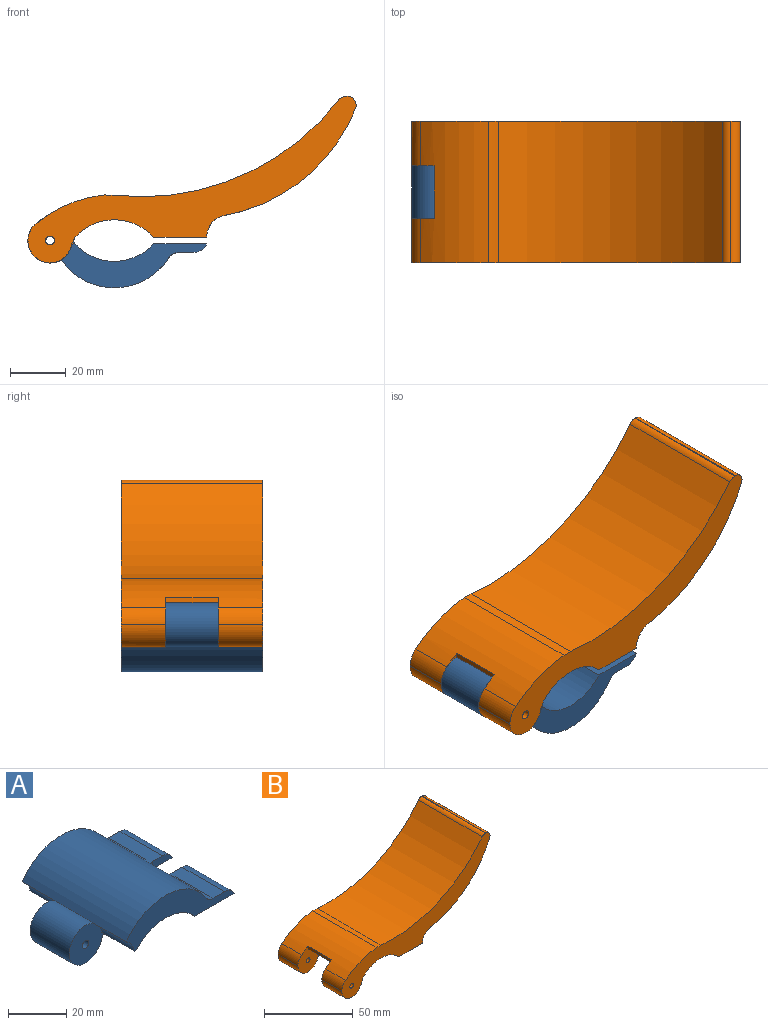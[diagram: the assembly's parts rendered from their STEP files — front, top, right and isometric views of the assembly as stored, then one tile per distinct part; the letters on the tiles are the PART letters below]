
ASSEMBLY  parts=2 mates=1
PART A: 23 faces, bbox 64.3x50.8x24.9 mm
  f0: cylinder r=23.18mm len=50.8mm, axis (0,1,0), area 2287.2mm2, adj f1,f2,f6,f10,f17,f20,f21,f22
  f1: cylinder r=4.04mm len=19.33mm, axis (0,1,0), area 75.8mm2, adj f0,f9,f10,f22
  f2: cylinder r=4.04mm len=19.33mm, axis (0,1,0), area 75.8mm2, adj f0,f6,f9,f22
  f3: cylinder r=4.76mm len=9.53mm, axis (0,0,-1), area 47.5mm2, adj f7,f9,f11,f12
  f4: plane 15.88x1.06mm, normal (0,0,-1), area 16.8mm2, adj f8,f10,f16,f21
  f5: plane 15.88x1.06mm, normal (0,0,-1), area 16.8mm2, adj f6,f8,f15,f20
  f6: plane 52.4x15.88mm, normal (0,-1,0), area 396.4mm2, adj f0,f2,f5,f7,f8,f9,f14,f20
  f7: plane 50.8x19.05mm, normal (0,0,-1), area 841.4mm2, adj f3,f6,f8,f10,f11,f12,f13,f14
  f8: cylinder r=19.05mm len=50.8mm, axis (0,1,0), area 1627.9mm2, adj f4,f5,f6,f7,f10,f19
  f9: plane 50.8x12.15mm, normal (0,0,1), area 273mm2, adj f1,f2,f3,f6,f10,f11,f12,f13
  f10: plane 52.4x15.88mm, normal (0,1,0), area 396.4mm2, adj f0,f1,f4,f7,f8,f9,f13,f21
  f11: plane 9.53x3.18mm, normal (0,-1,0), area 26.1mm2, adj f3,f7,f9,f13
  f12: plane 9.53x3.18mm, normal (0,1,0), area 26.1mm2, adj f3,f7,f9,f14
  f13: cylinder r=5.08mm len=20.64mm, axis (0,1,0), area 124.4mm2, adj f7,f9,f10,f11
  f14: cylinder r=5.08mm len=20.64mm, axis (0,1,0), area 124.4mm2, adj f6,f7,f9,f12
  f15: plane 16.85x15.88mm, normal (0,-1,0), area 191.4mm2, adj f5,f17,f18,f19,f20
  f16: plane 16.85x15.88mm, normal (0,1,0), area 191.4mm2, adj f4,f17,f18,f19,f21
  f17: cylinder r=7.94mm len=19.05mm, axis (0,-1,0), area 736.8mm2, adj f0,f15,f16,f19
  f18: cylinder r=1.59mm len=19.05mm, axis (0,-1,0), area 190mm2, adj f15,f16
  f19: plane 19.05x3.94mm, normal (0.93,0,-0.35), area 80.3mm2, adj f8,f15,f16,f17
  f20: cylinder r=7.94mm len=15.88mm, axis (0,1,0), area 114.1mm2, adj f0,f5,f6,f15
  f21: cylinder r=7.94mm len=15.88mm, axis (0,-1,0), area 114.1mm2, adj f0,f4,f10,f16
  f22: cylinder r=7.33mm len=14.6mm, axis (0,0,-1), area 70.7mm2, adj f0,f1,f2,f9
PART B: 41 faces, bbox 118x50.8x60.1 mm
  f0: plane 15.88x0.02mm, normal (0,0,-1), area 0.4mm2, adj f2,f11,f13,f21
  f1: cylinder r=1.59mm len=15.88mm, axis (0,-1,0), area 158.3mm2, adj f11,f21
  f2: cylinder r=8.03mm len=15.88mm, axis (0,1,0), area 111.6mm2, adj f0,f11,f21,f26
  f3: plane 118.05x60.07mm, normal (0,1,0), area 1573.9mm2, adj f5,f6,f9,f10,f12,f15,f17,f18
  f4: cylinder r=7.77mm len=20.64mm, axis (0,1,0), area 192.9mm2, adj f5,f8,f11,f29,f30,f34
  f5: cylinder r=62.96mm len=50.8mm, axis (0,1,0), area 3118.5mm2, adj f3,f4,f6,f11,f23,f27,f34,f35
  f6: cylinder r=7.77mm len=20.64mm, axis (0,1,0), area 195.6mm2, adj f3,f5,f10,f28,f30,f35
  f7: cylinder r=4.76mm len=9.53mm, axis (0,0,-1), area 47.5mm2, adj f9,f28,f29,f30
  f8: plane 20.64x0.54mm, normal (1,0,0), area 11mm2, adj f4,f9,f11,f29
  f9: plane 50.8x19.05mm, normal (0,0,-1), area 841.4mm2, adj f3,f7,f8,f10,f11,f19,f28,f29
  f10: plane 20.64x0.54mm, normal (1,0,0), area 11mm2, adj f3,f6,f9,f28
  f11: plane 118.03x59.86mm, normal (0,-1,0), area 1571mm2, adj f0,f1,f2,f4,f5,f8,f9,f12
  f12: cylinder r=50.8mm len=50.8mm, axis (0,1,0), area 179.2mm2, adj f3,f11,f18,f26
  f13: cylinder r=7.94mm len=15.88mm, axis (0,-1,0), area 350.2mm2, adj f0,f11,f20,f21
  f14: plane 17.81x16.88mm, normal (0,-1,0), area 197.7mm2, adj f15,f16,f22,f25,f26,f36,f37,f38
  f15: cylinder r=8.02mm len=15.88mm, axis (0,1,0), area 360mm2, adj f3,f14,f22,f36
  f16: plane 19.05x1.06mm, normal (0,0,-1), area 20.2mm2, adj f14,f19,f21,f38
  f17: plane 50.8x0.28mm, normal (0,0,1), area 14.2mm2, adj f3,f11,f23,f24
  f18: cylinder r=89.61mm len=80.77mm, axis (0,1,0), area 4659.5mm2, adj f3,f11,f12,f24
  f19: cylinder r=19.05mm len=50.8mm, axis (0,1,0), area 1627.9mm2, adj f3,f9,f11,f16,f20,f22
  f20: plane 15.88x3.94mm, normal (0.93,0,-0.35), area 66.9mm2, adj f11,f13,f19,f21
  f21: plane 17.67x16.88mm, normal (0,1,0), area 194.7mm2, adj f0,f1,f2,f13,f16,f20,f26,f37
  f22: plane 15.88x3.73mm, normal (0.95,0,-0.32), area 62.4mm2, adj f3,f14,f15,f19
  f23: cylinder r=3.3mm len=50.8mm, axis (0,1,0), area 327.9mm2, adj f3,f5,f11,f17
  f24: cylinder r=3.3mm len=50.8mm, axis (0,1,0), area 153.3mm2, adj f3,f11,f17,f18
  f25: cylinder r=1.59mm len=15.88mm, axis (0,1,0), area 158.3mm2, adj f3,f14
  f26: cylinder r=46.61mm len=50.8mm, axis (0,-1,0), area 1256mm2, adj f2,f3,f11,f12,f14,f21,f36,f37
  f27: plane 28.99x15.03mm, normal (0,0,-1), area 402.7mm2, adj f5,f31,f32,f33,f34,f35,f39,f40
  f28: plane 10.09x3.18mm, normal (0,-1,0), area 30.8mm2, adj f6,f7,f9,f10,f30
  f29: plane 10.09x3.18mm, normal (0,1,0), area 30.8mm2, adj f4,f7,f8,f9,f30
  f30: plane 16.44x15.03mm, normal (0,0,1), area 82.4mm2, adj f4,f6,f7,f28,f29,f31,f32,f33
  f31: plane 7.33x6.35mm, normal (1,0,0), area 46.6mm2, adj f27,f30,f32,f33
  f32: plane 6.35x5.3mm, normal (0.5,0.87,0), area 38.9mm2, adj f27,f30,f31,f40
  f33: plane 6.35x5.3mm, normal (0.5,-0.87,0), area 38.9mm2, adj f27,f30,f31,f39
  f34: plane 13.11x6.35mm, normal (0,1,0), area 27.7mm2, adj f4,f5,f27,f30,f40
  f35: plane 13.11x6.35mm, normal (0,-1,0), area 27.7mm2, adj f5,f6,f27,f30,f39
  f36: cylinder r=8.03mm len=15.88mm, axis (0,1,0), area 111.6mm2, adj f3,f14,f15,f26
  f37: plane 19.05x1.79mm, normal (-1,0,0), area 34.1mm2, adj f14,f21,f26,f38
  f38: cylinder r=7.94mm len=19.05mm, axis (0,-1,0), area 216mm2, adj f14,f16,f21,f37
  f39: plane 10.58x6.35mm, normal (0.06,-1,0), area 67.3mm2, adj f27,f30,f33,f35
  f40: plane 10.58x6.35mm, normal (0.09,1,0), area 67.4mm2, adj f27,f30,f32,f34
PLACE A rot(axis=(-1,0,0),180deg) t=(-29.99,-47.6,32.78)mm
PLACE B rot(axis=(0.91,0.21,-0.36),0deg) t=(-29.99,3.2,67.96)mm
MATE revolute A.f17 <-> B.f1  axis (0,1,0) through (-53.11,-31.73,50.37)mm
